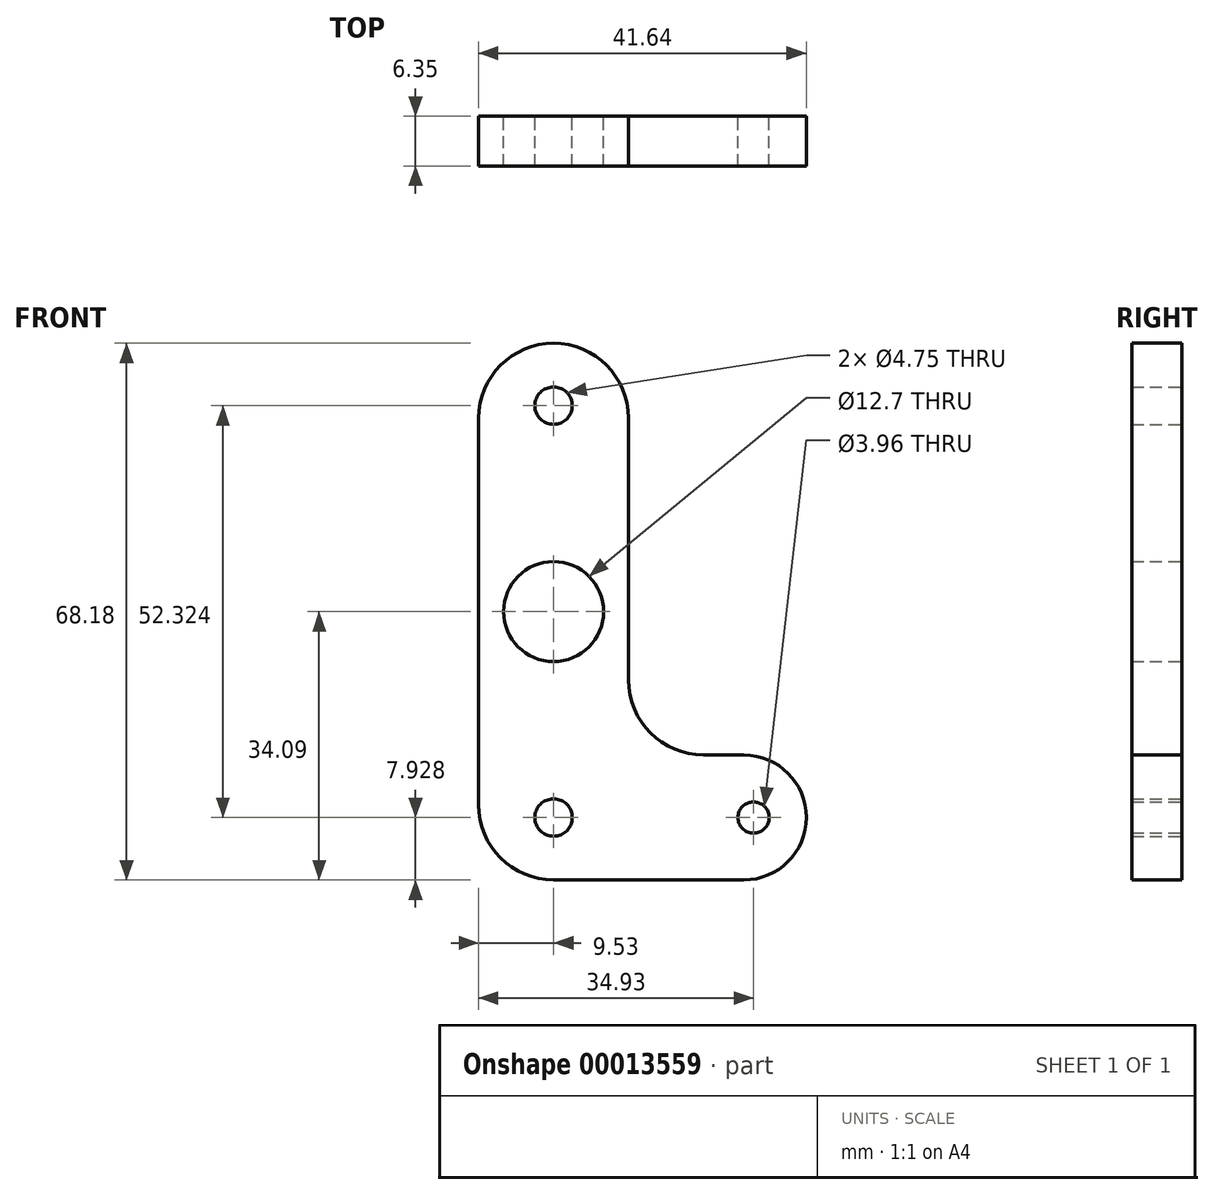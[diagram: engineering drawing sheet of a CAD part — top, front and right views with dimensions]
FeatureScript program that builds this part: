
annotation { "Feature Type Name" : "Feature", "Feature Type Description" : "" }
export const myFeature = defineFeature(function(context is Context, id is Id, definition is map)
    precondition{}
    {
        {
            var Q0;
            Q0=qCreatedBy(makeId("Front.planeOp"),FACE);
            var sketch = newSketch(context, id + "F0", { "sketchPlane" : qUnion([Q0])});
            skCircle(sketch, "E0", {"center": v(0, 0) * mm, "radius": 6.35 * mm});
            skCircle(sketch, "E1", {"center": v(0, 26.16) * mm, "radius": 2.37 * mm});
            skCircle(sketch, "E2", {"center": v(0, -26.16) * mm, "radius": 2.37 * mm});
            skLineSegment(sketch, "E3.bottom", {"start": v(-9.53, 34.09) * mm, "end": v(9.52, 34.09) * mm});
            skLineSegment(sketch, "E3.top", {"start": v(-9.52, -34.09) * mm, "end": v(9.53, -34.09) * mm});
            skLineSegment(sketch, "E3.left", {"start": v(-9.53, 34.09) * mm, "end": v(-9.52, -34.09) * mm});
            skLineSegment(sketch, "E3.right", {"start": v(9.52, 34.09) * mm, "end": v(9.53, -18.21) * mm});
            skCircle(sketch, "E4", {"center": v(25.4, -26.16) * mm, "radius": 1.98 * mm});
            skLineSegment(sketch, "E5", {"start": v(9.53, -34.09) * mm, "end": v(32.1, -34.09) * mm});
            skLineSegment(sketch, "E6", {"start": v(32.1, -34.09) * mm, "end": v(32.1, -18.21) * mm});
            skLineSegment(sketch, "E7", {"start": v(32.1, -18.21) * mm, "end": v(9.53, -18.21) * mm});
            skSolve(sketch);
        }
        {
            var Q0;
            Q0=makeQuery(id+"F0.imprint","IMPRINT",FACE,{"disambiguationData":[TD([[makeQuery(id+"F0.imprint","IMPRINT",EDGE,{"derivedFrom":sQuery(id+"F0.wireOp",EDGE,"E0")}),-1.0]])]});
            extrude(context, id + "F1", {"entities" : qUnion([Q0]), "depth" : 6.35 * mm});
        }
        {
            var Q0;
            Q0=makeQuery(id+"F1.opExtrude","SWEPT_EDGE",EDGE,{"disambiguationData":[OSD([sQuery(id+"F0.wireOp",EDGE,"E3.bottom"),sQuery(id+"F0.wireOp",EDGE,"E3.left")])]});
            var Q1;
            Q1=makeQuery(id+"F1.opExtrude","SWEPT_EDGE",EDGE,{"disambiguationData":[OSD([sQuery(id+"F0.wireOp",EDGE,"E3.bottom"),sQuery(id+"F0.wireOp",EDGE,"E3.right")])]});
            var Q2;
            Q2=makeQuery(id+"F1.opExtrude","SWEPT_EDGE",EDGE,{"disambiguationData":[OSD([sQuery(id+"F0.wireOp",EDGE,"E3.top"),sQuery(id+"F0.wireOp",EDGE,"E3.left")])]});
            var Q3;
            Q3=makeQuery(id+"F1.opExtrude","SWEPT_EDGE",EDGE,{"disambiguationData":[OSD([sQuery(id+"F0.wireOp",EDGE,"E3.right"),sQuery(id+"F0.wireOp",EDGE,"E7")])]});
            fillet(context, id + "F2", {"entities" : qUnion([Q0, Q1, Q2, Q3]), "radius" : 9.52 * mm, "tangentPropagation" : true, "allowEdgeOverflow" : false});
        }
        {
            var Q0;
            Q0=makeQuery(id+"F1.opExtrude","SWEPT_EDGE",EDGE,{"disambiguationData":[OSD([sQuery(id+"F0.wireOp",EDGE,"E6"),sQuery(id+"F0.wireOp",EDGE,"E7")])]});
            var Q1;
            Q1=makeQuery(id+"F1.opExtrude","SWEPT_EDGE",EDGE,{"disambiguationData":[OSD([sQuery(id+"F0.wireOp",EDGE,"E5"),sQuery(id+"F0.wireOp",EDGE,"E6")])]});
            fillet(context, id + "F3", {"entities" : qUnion([Q0, Q1]), "radius" : 7.94 * mm, "tangentPropagation" : true, "allowEdgeOverflow" : false});
        }
    });
